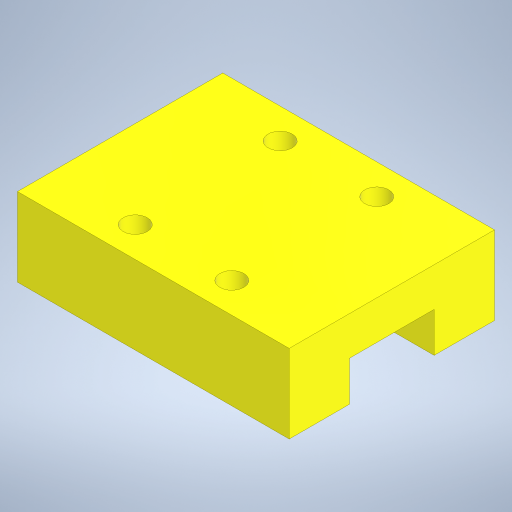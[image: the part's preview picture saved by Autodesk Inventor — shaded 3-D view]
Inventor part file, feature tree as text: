
AUTODESK INVENTOR PART (.ipt)
format: ipt  version: 2024 (Build 280153000, 153)  size: 222,208 bytes
history: native  units: mm
features: extrude x2, sketch x2
ambient origin geometry x8: Origin, YZ Plane, XZ Plane, XY Plane, X Axis, Y Axis, Z Axis, Center Point
bodies: Solid1 (feature_tree)
feature tree (4):
  extrude  "Extrusion1"  Depth=3.3mm
  extrude  "Extrusion2"  Depth=5.0mm
  sketch  "Sketch1"  dims[d0=17.0mm d1=3.3mm]
  sketch  "Sketch2"  dims[d2=6.5mm d3=5.0mm d4=7.0mm d5=22.5mm d6=0.0mm d7=8.0mm d8=2.0mm d10=2.0mm d12=2.0mm d13=2.0mm d14=12.0mm d15=12.0mm d16=2.5mm d17=7.25mm d18=7.25mm d20=8.0mm d21=2.5mm d22=0.0mm d23=0.0mm]
